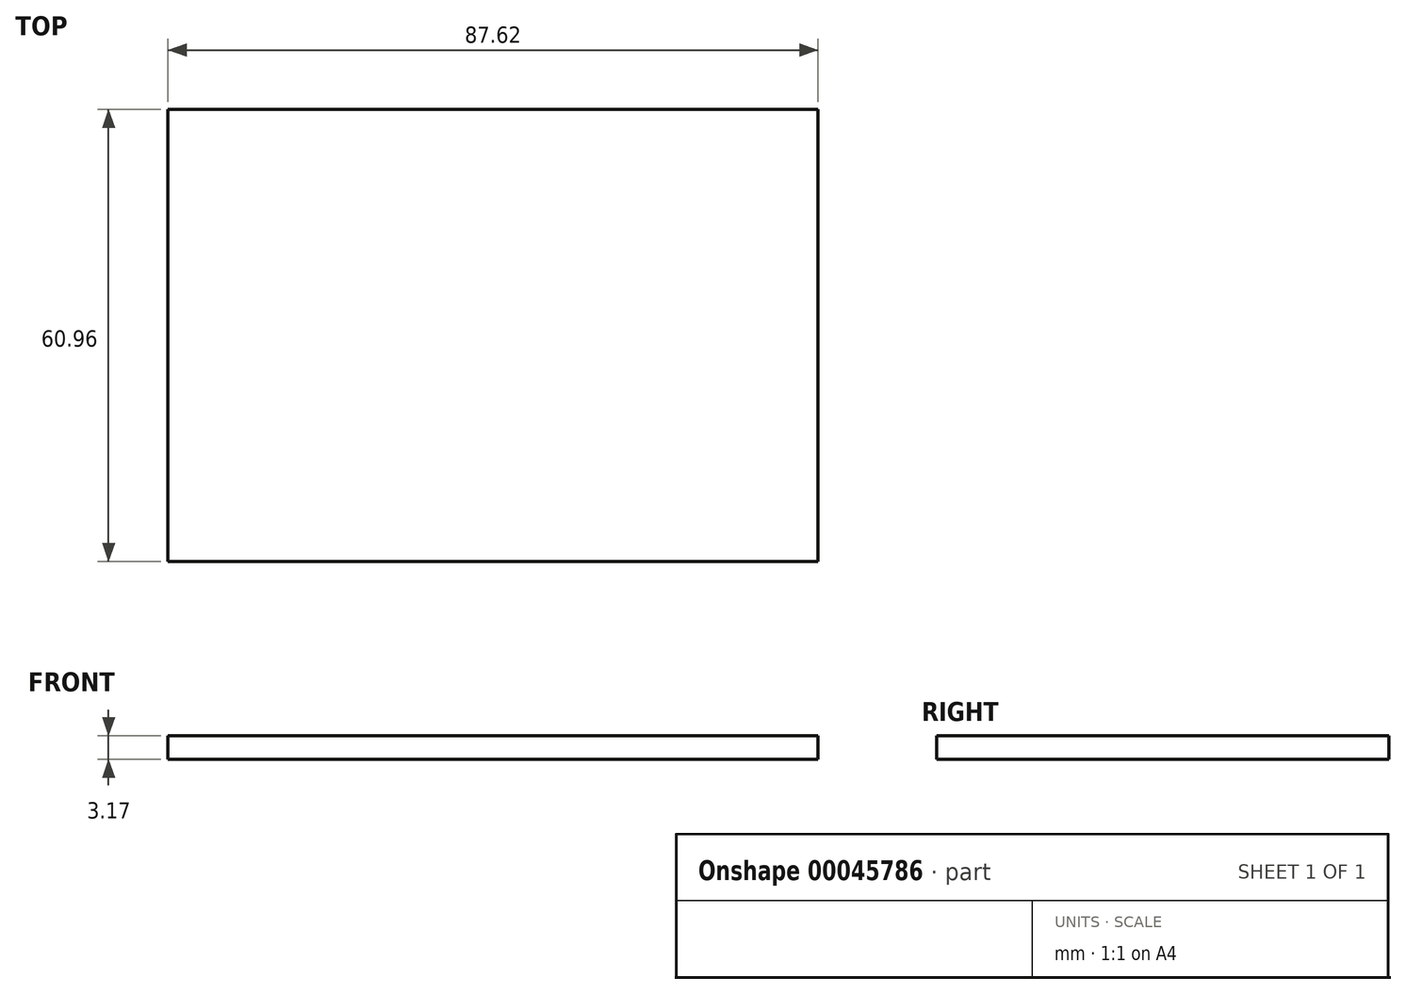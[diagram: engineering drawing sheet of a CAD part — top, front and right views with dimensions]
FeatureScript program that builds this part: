
annotation { "Feature Type Name" : "Feature", "Feature Type Description" : "" }
export const myFeature = defineFeature(function(context is Context, id is Id, definition is map)
    precondition{}
    {
        {
            var Q0;
            Q0=qCreatedBy(makeId("Top.planeOp"),FACE);
            var sketch = newSketch(context, id + "F0", { "sketchPlane" : qUnion([Q0])});
            skLineSegment(sketch, "E0.rect.bottom", {"start": v(-43.81, 30.48) * mm, "end": v(43.82, 30.48) * mm});
            skLineSegment(sketch, "E0.rect.top", {"start": v(-43.82, -30.48) * mm, "end": v(43.81, -30.48) * mm});
            skLineSegment(sketch, "E0.rect.left", {"start": v(-43.81, 30.48) * mm, "end": v(-43.82, -30.48) * mm});
            skLineSegment(sketch, "E0.rect.right", {"start": v(43.82, 30.48) * mm, "end": v(43.81, -30.48) * mm});
            skPoint(sketch, "E0.rect.middle", {"position": v(0, 0) * mm});
            skSolve(sketch);
        }
        {
            var Q0;
            Q0 = qSketchRegion(id + "F0", true);
            extrude(context, id + "F1", {"entities" : qUnion([Q0]), "depth" : 3.17 * mm});
        }
    });
